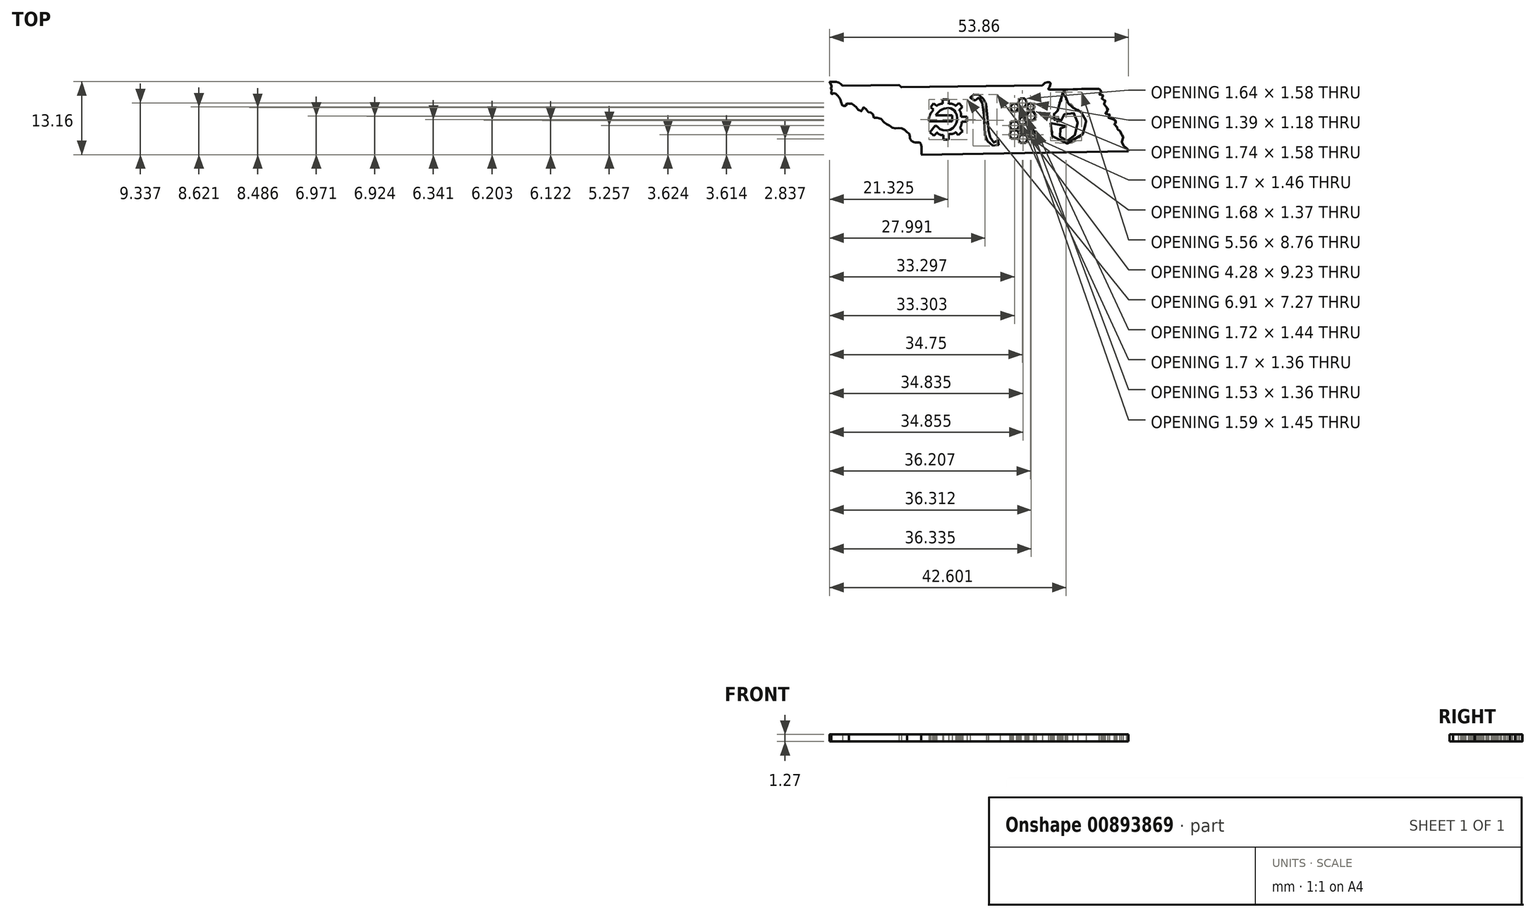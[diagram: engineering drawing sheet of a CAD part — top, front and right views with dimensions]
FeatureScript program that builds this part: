
annotation { "Feature Type Name" : "Feature", "Feature Type Description" : "" }
export const myFeature = defineFeature(function(context is Context, id is Id, definition is map)
    precondition{}
    {
        {
            var Q0;
            Q0=qCreatedBy(makeId("Top.planeOp"),FACE);
            var sketch = newSketch(context, id + "F0", { "sketchPlane" : qUnion([Q0])});
            skLineSegment(sketch, "E0", {"start": v(-39.27, 28.7) * mm, "end": v(-40.07, 28.7) * mm});
            skLineSegment(sketch, "E1", {"start": v(-40.07, 28.7) * mm, "end": v(-40.5, 27.94) * mm});
            skLineSegment(sketch, "E2", {"start": v(-40.5, 27.94) * mm, "end": v(-40.07, 27.12) * mm});
            skLineSegment(sketch, "E3", {"start": v(-39.27, 28.7) * mm, "end": v(-38.86, 27.94) * mm});
            skLineSegment(sketch, "E4", {"start": v(-38.86, 27.94) * mm, "end": v(-39.27, 27.22) * mm});
            skLineSegment(sketch, "E5", {"start": v(-40.07, 27.12) * mm, "end": v(-39.27, 27.22) * mm});
            skLineSegment(sketch, "E6", {"start": v(-40.69, 27.78) * mm, "end": v(-40.34, 27.12) * mm});
            skLineSegment(sketch, "E7", {"start": v(-40.34, 27.12) * mm, "end": v(-40.79, 26.33) * mm});
            skLineSegment(sketch, "E8", {"start": v(-40.69, 27.78) * mm, "end": v(-41.36, 27.78) * mm});
            skLineSegment(sketch, "E9", {"start": v(-41.36, 27.78) * mm, "end": v(-41.93, 27.12) * mm});
            skLineSegment(sketch, "E10", {"start": v(-41.93, 27.12) * mm, "end": v(-41.52, 26.33) * mm});
            skLineSegment(sketch, "E11", {"start": v(-40.79, 26.33) * mm, "end": v(-41.52, 26.33) * mm});
            skLineSegment(sketch, "E12", {"start": v(-37.75, 27.78) * mm, "end": v(-38.6, 27.78) * mm});
            skLineSegment(sketch, "E13", {"start": v(-38.6, 27.78) * mm, "end": v(-38.92, 27.22) * mm});
            skLineSegment(sketch, "E14", {"start": v(-38.92, 27.22) * mm, "end": v(-38.6, 26.6) * mm});
            skLineSegment(sketch, "E15", {"start": v(-37.75, 27.78) * mm, "end": v(-37.53, 27.22) * mm});
            skLineSegment(sketch, "E16", {"start": v(-37.53, 27.22) * mm, "end": v(-37.75, 26.64) * mm});
            skLineSegment(sketch, "E17", {"start": v(-37.75, 26.64) * mm, "end": v(-38.6, 26.6) * mm});
            skLineSegment(sketch, "E18", {"start": v(-37.75, 26.33) * mm, "end": v(-38.6, 26.3) * mm});
            skLineSegment(sketch, "E19", {"start": v(-37.75, 26.33) * mm, "end": v(-37.25, 25.55) * mm});
            skLineSegment(sketch, "E20", {"start": v(-38.6, 26.3) * mm, "end": v(-39, 25.6) * mm});
            skLineSegment(sketch, "E21", {"start": v(-37.25, 25.55) * mm, "end": v(-37.7, 24.75) * mm});
            skLineSegment(sketch, "E22", {"start": v(-39, 25.6) * mm, "end": v(-38.67, 24.76) * mm});
            skLineSegment(sketch, "E23", {"start": v(-37.7, 24.75) * mm, "end": v(-38.67, 24.76) * mm});
            skLineSegment(sketch, "E24", {"start": v(-39.11, 25.37) * mm, "end": v(-38.83, 24.63) * mm});
            skPoint(sketch, "E24.endSnap0", {"position": v(-38.83, 25.18) * mm});
            skLineSegment(sketch, "E25", {"start": v(-38.83, 24.63) * mm, "end": v(-39.18, 24.01) * mm});
            skLineSegment(sketch, "E26", {"start": v(-39.11, 25.37) * mm, "end": v(-39.94, 25.37) * mm});
            skLineSegment(sketch, "E27", {"start": v(-39.94, 25.37) * mm, "end": v(-40.36, 24.63) * mm});
            skLineSegment(sketch, "E28", {"start": v(-40.36, 24.63) * mm, "end": v(-40.13, 24.03) * mm});
            skLineSegment(sketch, "E29", {"start": v(-39.18, 24.01) * mm, "end": v(-40.13, 24.03) * mm});
            skLineSegment(sketch, "E30", {"start": v(-40.54, 24.5) * mm, "end": v(-40.28, 23.82) * mm});
            skLineSegment(sketch, "E31", {"start": v(-40.28, 23.82) * mm, "end": v(-40.6, 23.2) * mm});
            skLineSegment(sketch, "E32", {"start": v(-40.54, 24.5) * mm, "end": v(-41.6, 24.5) * mm});
            skLineSegment(sketch, "E33", {"start": v(-41.6, 24.5) * mm, "end": v(-41.98, 23.82) * mm});
            skLineSegment(sketch, "E34", {"start": v(-41.98, 23.82) * mm, "end": v(-41.72, 23.15) * mm});
            skLineSegment(sketch, "E35", {"start": v(-40.6, 23.2) * mm, "end": v(-41.72, 23.15) * mm});
            skLineSegment(sketch, "E36", {"start": v(-40.6, 22.92) * mm, "end": v(-41.72, 22.85) * mm});
            skLineSegment(sketch, "E37", {"start": v(-40.6, 22.92) * mm, "end": v(-40.28, 22.3) * mm});
            skLineSegment(sketch, "E38", {"start": v(-40.28, 22.3) * mm, "end": v(-40.6, 21.47) * mm});
            skLineSegment(sketch, "E39", {"start": v(-41.72, 22.85) * mm, "end": v(-41.98, 22.15) * mm});
            skLineSegment(sketch, "E40", {"start": v(-41.98, 22.15) * mm, "end": v(-41.72, 21.47) * mm});
            skLineSegment(sketch, "E41", {"start": v(-40.6, 21.47) * mm, "end": v(-41.72, 21.47) * mm});
            skLineSegment(sketch, "E42", {"start": v(-39.08, 22.1) * mm, "end": v(-40.08, 22.1) * mm});
            skLineSegment(sketch, "E43", {"start": v(-40.08, 22.1) * mm, "end": v(-40.41, 21.36) * mm});
            skLineSegment(sketch, "E44", {"start": v(-40.41, 21.36) * mm, "end": v(-40.08, 20.73) * mm});
            skLineSegment(sketch, "E45", {"start": v(-39.08, 22.1) * mm, "end": v(-38.74, 21.47) * mm});
            skLineSegment(sketch, "E46", {"start": v(-38.74, 21.47) * mm, "end": v(-39.08, 20.72) * mm});
            skLineSegment(sketch, "E47", {"start": v(-39.08, 20.72) * mm, "end": v(-40.08, 20.73) * mm});
            skLineSegment(sketch, "E48", {"start": v(-37.57, 22.9) * mm, "end": v(-37.24, 22.24) * mm});
            skLineSegment(sketch, "E49", {"start": v(-37.24, 22.24) * mm, "end": v(-37.63, 21.47) * mm});
            skLineSegment(sketch, "E50", {"start": v(-37.57, 22.9) * mm, "end": v(-38.55, 22.9) * mm});
            skLineSegment(sketch, "E51", {"start": v(-38.55, 22.9) * mm, "end": v(-38.95, 22.17) * mm});
            skLineSegment(sketch, "E52", {"start": v(-38.95, 22.17) * mm, "end": v(-38.6, 21.5) * mm});
            skLineSegment(sketch, "E53", {"start": v(-37.63, 21.47) * mm, "end": v(-38.6, 21.5) * mm});
            skLineSegment(sketch, "E54", {"start": v(-52.37, 25.66) * mm, "end": v(-52.37, 24.59) * mm});
            skLineSegment(sketch, "E55", {"start": v(-52.37, 25.66) * mm, "end": v(-55.36, 25.66) * mm});
            skLineSegment(sketch, "E56", {"start": v(-52.37, 24.59) * mm, "end": v(-56.43, 24.59) * mm});
            skFitSpline(sketch, "E57", {"points": [v(-56.43, 24.59) * mm, v(-56.54, 24.72) * mm, v(-56.43, 25.58) * mm, v(-55.9, 26.42) * mm], "startDerivative": vector(-0.75, 0.5) * mm, "endDerivative": vector(1.41, 1.79) * mm});
            skLineSegment(sketch, "E58", {"start": v(-55.13, 27.37) * mm, "end": v(-55.68, 27.8) * mm});
            skLineSegment(sketch, "E59", {"start": v(-55.68, 27.8) * mm, "end": v(-56.24, 27.1) * mm});
            skLineSegment(sketch, "E60", {"start": v(-56.24, 27.1) * mm, "end": v(-55.73, 26.7) * mm});
            skLineSegment(sketch, "E61", {"start": v(-52.97, 27.73) * mm, "end": v(-52.97, 28.54) * mm});
            skLineSegment(sketch, "E62", {"start": v(-52.97, 28.54) * mm, "end": v(-54.04, 28.54) * mm});
            skLineSegment(sketch, "E63", {"start": v(-54.04, 28.54) * mm, "end": v(-54.04, 27.75) * mm});
            skLineSegment(sketch, "E64", {"start": v(-50.5, 27.18) * mm, "end": v(-51.09, 26.62) * mm});
            skLineSegment(sketch, "E65", {"start": v(-50.5, 27.18) * mm, "end": v(-51.16, 27.88) * mm});
            skLineSegment(sketch, "E66", {"start": v(-51.16, 27.88) * mm, "end": v(-51.72, 27.35) * mm});
            skLineSegment(sketch, "E67", {"start": v(-49.65, 25.43) * mm, "end": v(-49.65, 24.53) * mm});
            skLineSegment(sketch, "E68", {"start": v(-49.65, 24.53) * mm, "end": v(-50.33, 24.53) * mm});
            skLineSegment(sketch, "E69", {"start": v(-49.65, 25.43) * mm, "end": v(-50.32, 25.43) * mm});
            skLineSegment(sketch, "E70", {"start": v(-50.93, 23.39) * mm, "end": v(-50.46, 22.78) * mm});
            skLineSegment(sketch, "E71", {"start": v(-50.46, 22.78) * mm, "end": v(-51.29, 22.13) * mm});
            skLineSegment(sketch, "E72", {"start": v(-51.29, 22.13) * mm, "end": v(-51.69, 22.65) * mm});
            skLineSegment(sketch, "E73", {"start": v(-52.99, 22.09) * mm, "end": v(-52.99, 21.28) * mm});
            skLineSegment(sketch, "E74", {"start": v(-52.99, 21.28) * mm, "end": v(-53.96, 21.28) * mm});
            skLineSegment(sketch, "E75", {"start": v(-53.96, 21.28) * mm, "end": v(-53.96, 22.1) * mm});
            skLineSegment(sketch, "E76", {"start": v(-55.12, 22.5) * mm, "end": v(-55.63, 21.98) * mm});
            skLineSegment(sketch, "E77", {"start": v(-55.63, 21.98) * mm, "end": v(-56.37, 22.6) * mm});
            skLineSegment(sketch, "E78", {"start": v(-56.37, 22.6) * mm, "end": v(-55.38, 23.8) * mm});
            skFitSpline(sketch, "E79", {"points": [v(-55.73, 26.7) * mm, v(-55.9, 26.42) * mm], "startDerivative": vector(-0.18, -0.28) * mm, "endDerivative": vector(-0.18, -0.28) * mm});
            skFitSpline(sketch, "E80", {"points": [v(-54.04, 27.75) * mm, v(-54.32, 27.75) * mm, v(-54.62, 27.66) * mm, v(-54.9, 27.54) * mm, v(-55.13, 27.37) * mm], "startDerivative": vector(-1.13, 0.08) * mm, "endDerivative": vector(-0.94, -0.73) * mm});
            skPoint(sketch, "E81.2.internal.snap0", {"position": v(-50.83, 27.53) * mm});
            skFitSpline(sketch, "E81", {"points": [v(-51.72, 27.35) * mm, v(-51.83, 27.46) * mm, v(-51.94, 27.53) * mm, v(-52.16, 27.64) * mm, v(-52.51, 27.75) * mm, v(-52.76, 27.75) * mm, v(-52.97, 27.73) * mm], "startDerivative": vector(-0.84, 0.83) * mm, "endDerivative": vector(-1.27, -0.15) * mm});
            skFitSpline(sketch, "E82", {"points": [v(-51.09, 26.62) * mm, v(-50.99, 26.52) * mm, v(-50.93, 26.43) * mm, v(-50.87, 26.32) * mm, v(-50.82, 26.17) * mm, v(-50.78, 26) * mm, v(-50.77, 25.83) * mm, v(-50.75, 25.66) * mm, v(-50.75, 25.53) * mm, v(-50.76, 25.43) * mm], "startDerivative": vector(0.92, -0.94) * mm, "endDerivative": vector(-0.13, -1.07) * mm});
            skLineSegment(sketch, "E83", {"start": v(-50.32, 25.43) * mm, "end": v(-50.76, 25.43) * mm});
            skLineSegment(sketch, "E84", {"start": v(-50.33, 24.53) * mm, "end": v(-50.6, 24.53) * mm});
            skFitSpline(sketch, "E85", {"points": [v(-50.6, 24.53) * mm, v(-50.6, 24.48) * mm, v(-50.6, 24.42) * mm, v(-50.6, 24.34) * mm, v(-50.63, 24.21) * mm, v(-50.66, 24.13) * mm, v(-50.67, 24) * mm, v(-50.7, 23.9) * mm, v(-50.77, 23.76) * mm, v(-50.8, 23.67) * mm, v(-50.85, 23.57) * mm, v(-50.9, 23.5) * mm, v(-50.9, 23.45) * mm, v(-50.93, 23.39) * mm], "startDerivative": vector(0, -0.85) * mm, "endDerivative": vector(-0.45, -0.89) * mm});
            skFitSpline(sketch, "E86", {"points": [v(-51.69, 22.65) * mm, v(-51.76, 22.58) * mm, v(-51.9, 22.46) * mm, v(-52.11, 22.36) * mm, v(-52.38, 22.29) * mm, v(-52.65, 22.29) * mm, v(-52.85, 22.33) * mm, v(-52.99, 22.09) * mm], "startDerivative": vector(-0.64, -0.65) * mm, "endDerivative": vector(-0.73, -1.97) * mm});
            skFitSpline(sketch, "E87", {"points": [v(-53.96, 22.1) * mm, v(-54.08, 22.1) * mm, v(-54.3, 22.1) * mm, v(-54.53, 22.17) * mm, v(-54.72, 22.26) * mm, v(-54.93, 22.41) * mm, v(-55.06, 22.56) * mm, v(-55.12, 22.5) * mm], "startDerivative": vector(-0.95, 0.02) * mm, "endDerivative": vector(-0.68, -0.94) * mm});
            skFitSpline(sketch, "E88", {"points": [v(-55.38, 23.8) * mm, v(-55.3, 23.9) * mm, v(-55.23, 23.93) * mm, v(-55.12, 23.8) * mm, v(-54.98, 23.62) * mm, v(-54.84, 23.47) * mm, v(-54.76, 23.39) * mm, v(-54.63, 23.24) * mm, v(-54.52, 23.17) * mm, v(-54.39, 23.1) * mm, v(-54.25, 23.04) * mm, v(-54.06, 22.99) * mm, v(-53.85, 22.96) * mm, v(-53.6, 22.93) * mm, v(-53.4, 22.95) * mm, v(-53.23, 22.97) * mm, v(-53.05, 23) * mm, v(-52.85, 23.03) * mm, v(-52.7, 23.05) * mm, v(-52.5, 23.1) * mm, v(-52.4, 23.17) * mm, v(-52.28, 23.25) * mm, v(-52.15, 23.39) * mm, v(-52, 23.53) * mm, v(-51.9, 23.68) * mm, v(-51.82, 23.8) * mm, v(-51.76, 23.93) * mm, v(-51.69, 24.08) * mm, v(-51.65, 24.19) * mm, v(-51.61, 24.3) * mm, v(-51.56, 24.44) * mm, v(-51.53, 24.53) * mm, v(-51.5, 24.64) * mm, v(-51.5, 24.72) * mm, v(-51.48, 24.8) * mm, v(-51.47, 24.9) * mm, v(-51.47, 24.98) * mm, v(-51.47, 25.09) * mm, v(-51.48, 25.17) * mm, v(-51.48, 25.23) * mm, v(-51.5, 25.32) * mm, v(-51.5, 25.4) * mm, v(-51.51, 25.53) * mm, v(-51.52, 25.66) * mm, v(-51.57, 25.81) * mm, v(-51.6, 25.97) * mm, v(-51.69, 26.13) * mm, v(-51.73, 26.2) * mm, v(-51.75, 26.24) * mm, v(-51.78, 26.3) * mm, v(-51.8, 26.34) * mm, v(-51.83, 26.38) * mm, v(-51.88, 26.43) * mm, v(-51.94, 26.5) * mm, v(-51.98, 26.54) * mm, v(-52.03, 26.59) * mm, v(-52.08, 26.63) * mm, v(-52.15, 26.68) * mm, v(-52.2, 26.7) * mm, v(-52.25, 26.74) * mm, v(-52.29, 26.76) * mm, v(-52.35, 26.8) * mm, v(-52.4, 26.82) * mm, v(-52.45, 26.85) * mm, v(-52.5, 26.88) * mm, v(-52.6, 26.92) * mm, v(-52.66, 26.94) * mm, v(-52.73, 26.96) * mm, v(-52.81, 26.96) * mm, v(-52.9, 26.97) * mm, v(-52.97, 26.98) * mm, v(-53.05, 26.99) * mm, v(-53.13, 26.98) * mm, v(-53.17, 26.98) * mm, v(-53.25, 26.97) * mm, v(-53.3, 26.96) * mm, v(-53.38, 26.95) * mm, v(-53.42, 26.95) * mm, v(-53.5, 26.93) * mm, v(-53.56, 26.92) * mm, v(-53.62, 26.9) * mm, v(-53.7, 26.9) * mm, v(-53.78, 26.87) * mm, v(-53.84, 26.85) * mm, v(-53.9, 26.83) * mm, v(-53.98, 26.8) * mm, v(-54.02, 26.79) * mm, v(-54.09, 26.76) * mm, v(-54.15, 26.74) * mm, v(-54.2, 26.71) * mm, v(-54.26, 26.68) * mm, v(-54.32, 26.66) * mm, v(-54.39, 26.61) * mm, v(-54.45, 26.57) * mm, v(-54.5, 26.52) * mm, v(-54.55, 26.5) * mm, v(-54.61, 26.46) * mm, v(-54.67, 26.42) * mm, v(-54.7, 26.38) * mm, v(-54.75, 26.34) * mm, v(-54.8, 26.3) * mm, v(-54.84, 26.26) * mm, v(-54.9, 26.21) * mm, v(-54.95, 26.16) * mm, v(-55, 26.1) * mm, v(-55.08, 26) * mm, v(-55.18, 25.89) * mm, v(-55.2, 25.84) * mm, v(-55.26, 25.78) * mm, v(-55.3, 25.72) * mm, v(-55.36, 25.66) * mm], "startDerivative": vector(7.58, 10.82) * mm, "endDerivative": vector(-6.43, -7.93) * mm});
            skPoint(sketch, "E89.35.internal.snap0", {"position": v(-49.65, 24.98) * mm});
            skPoint(sketch, "E89.80.internal.snap0", {"position": v(-49.65, 24.98) * mm});
            skFitSpline(sketch, "E89", {"points": [v(-47.5, 28.9) * mm, v(-47.69, 28.99) * mm, v(-47.87, 28.93) * mm, v(-47.92, 28.66) * mm, v(-48.16, 28.37) * mm, v(-48.48, 28.32) * mm, v(-48.77, 28.38) * mm, v(-49.01, 28.59) * mm, v(-49.08, 28.79) * mm, v(-49.04, 29.03) * mm, v(-48.97, 29.15) * mm, v(-48.85, 29.29) * mm, v(-48.74, 29.36) * mm, v(-48.52, 29.4) * mm, v(-48.4, 29.44) * mm, v(-48.18, 29.44) * mm, v(-47.97, 29.43) * mm, v(-47.73, 29.39) * mm, v(-47.53, 29.32) * mm, v(-47.36, 29.25) * mm, v(-47.15, 29.03) * mm, v(-46.97, 28.9) * mm, v(-46.77, 28.63) * mm, v(-46.58, 28.43) * mm, v(-46.48, 28.28) * mm, v(-46.39, 28.06) * mm, v(-46.3, 27.86) * mm, v(-46.24, 27.63) * mm, v(-46.17, 27.29) * mm, v(-46.16, 26.93) * mm, v(-46.11, 26.7) * mm, v(-46.1, 26.3) * mm, v(-46.08, 26.08) * mm, v(-46.04, 25.66) * mm, v(-46.04, 25.43) * mm, v(-46, 24.98) * mm, v(-45.96, 24.64) * mm, v(-45.94, 24.42) * mm, v(-45.88, 24.07) * mm, v(-45.88, 23.8) * mm, v(-45.84, 23.55) * mm, v(-45.84, 23.39) * mm, v(-45.8, 23.1) * mm, v(-45.76, 22.78) * mm, v(-45.72, 22.29) * mm, v(-45.62, 21.98) * mm, v(-45.5, 21.67) * mm, v(-45.37, 21.36) * mm, v(-45.16, 21) * mm, v(-44.93, 20.66) * mm, v(-44.83, 20.87) * mm, v(-44.72, 21) * mm, v(-44.6, 21.1) * mm, v(-44.37, 21.14) * mm, v(-44.18, 21.16) * mm, v(-43.96, 21.11) * mm, v(-43.8, 21.01) * mm, v(-43.72, 20.78) * mm, v(-43.82, 20.5) * mm, v(-44.03, 20.3) * mm, v(-44.2, 20.18) * mm, v(-44.48, 20.16) * mm, v(-44.83, 20.2) * mm, v(-45.05, 20.23) * mm, v(-45.32, 20.4) * mm, v(-45.58, 20.62) * mm, v(-45.88, 20.88) * mm, v(-46.03, 21.11) * mm, v(-46.18, 21.36) * mm, v(-46.3, 21.65) * mm, v(-46.39, 21.98) * mm, v(-46.45, 22.5) * mm, v(-46.45, 22.65) * mm, v(-46.47, 23.1) * mm, v(-46.5, 23.58) * mm, v(-46.5, 23.68) * mm, v(-46.5, 23.93) * mm, v(-46.53, 24.16) * mm, v(-46.55, 24.42) * mm, v(-46.56, 24.64) * mm, v(-46.57, 24.98) * mm, v(-46.6, 25.28) * mm, v(-46.61, 25.53) * mm, v(-46.64, 25.77) * mm, v(-46.67, 25.98) * mm, v(-46.7, 26.2) * mm, v(-46.74, 26.41) * mm, v(-46.77, 26.57) * mm, v(-46.8, 26.96) * mm, v(-46.85, 27.42) * mm, v(-46.9, 27.7) * mm, v(-46.97, 28.02) * mm, v(-47.1, 28.3) * mm, v(-47.2, 28.48) * mm, v(-47.35, 28.72) * mm, v(-47.5, 28.9) * mm]});
            skLineSegment(sketch, "E90", {"start": v(-31.8, 23.69) * mm, "end": v(-34.6, 24.27) * mm});
            skFitSpline(sketch, "E91", {"points": [v(-31.8, 23.69) * mm, v(-31.63, 23.48) * mm, v(-31.8, 23.42) * mm, v(-32.27, 23.46) * mm, v(-32.54, 23.47) * mm, v(-32.84, 23.34) * mm, v(-32.9, 23.22) * mm, v(-32.9, 22.78) * mm, v(-32.93, 22.54) * mm, v(-32.9, 22.2) * mm, v(-32.9, 21.77) * mm, v(-32.78, 21.59) * mm, v(-32.5, 21.36) * mm, v(-32.1, 21.16) * mm, v(-31.92, 21.13) * mm, v(-31.6, 21.08) * mm, v(-31.32, 21.12) * mm, v(-30.92, 21.36) * mm, v(-30.6, 21.6) * mm, v(-30.31, 22) * mm, v(-30.07, 22.42) * mm, v(-29.86, 23.18) * mm, v(-29.77, 23.92) * mm, v(-29.77, 24.48) * mm, v(-29.87, 24.92) * mm, v(-30.05, 25.45) * mm, v(-30.24, 25.83) * mm, v(-30.53, 26.14) * mm, v(-30.86, 26.2) * mm, v(-31.43, 26.21) * mm, v(-31.8, 25.98) * mm, v(-32.27, 25.78) * mm, v(-32.42, 25.54) * mm, v(-32.41, 25.39) * mm, v(-32.65, 25.29) * mm, v(-32.61, 25.06) * mm, v(-32.7, 24.78) * mm, v(-32.83, 24.46) * mm, v(-33.06, 24.4) * mm, v(-33.27, 24.45) * mm, v(-33.42, 24.53) * mm, v(-33.38, 24.72) * mm, v(-33.21, 25.03) * mm, v(-33.13, 25.17) * mm, v(-33.16, 25.41) * mm, v(-33.39, 25.37) * mm, v(-33.61, 25.2) * mm, v(-33.9, 24.81) * mm, v(-34.32, 24.86) * mm, v(-34.4, 25.17) * mm, v(-34.13, 25.46) * mm, v(-33.96, 25.66) * mm, v(-34.05, 25.97) * mm, v(-33.97, 26.2) * mm, v(-33.8, 26.13) * mm, v(-33.58, 26.07) * mm, v(-33.39, 26.08) * mm, v(-33.33, 26.3) * mm, v(-33.27, 26.75) * mm, v(-33.1, 26.88) * mm, v(-33.14, 27.37) * mm, v(-33.05, 27.82) * mm, v(-32.9, 28.1) * mm, v(-32.73, 28.22) * mm, v(-32.7, 28.45) * mm, v(-32.63, 28.9) * mm, v(-32.54, 29.23) * mm, v(-32.46, 29.72) * mm, v(-32.43, 29.83) * mm, v(-32.13, 29.88) * mm, v(-31.8, 29.81) * mm, v(-31.8, 29.48) * mm, v(-31.99, 28.28) * mm, v(-31.8, 28.04) * mm, v(-31.57, 27.98) * mm, v(-31.61, 27.7) * mm, v(-31.5, 27.8) * mm, v(-31.24, 27.86) * mm, v(-30.98, 27.8) * mm, v(-30.78, 27.73) * mm, v(-30.63, 27.5) * mm, v(-30.6, 27.25) * mm, v(-30.6, 27.04) * mm, v(-30.39, 27.09) * mm, v(-29.75, 26.9) * mm, v(-29.43, 26.59) * mm, v(-29.13, 26.24) * mm, v(-28.91, 25.9) * mm, v(-28.7, 25.53) * mm, v(-28.43, 25.13) * mm, v(-28.25, 24.74) * mm, v(-28.24, 24.3) * mm, v(-28.31, 23.5) * mm, v(-28.58, 22.7) * mm, v(-29.37, 21.58) * mm, v(-30.5, 20.74) * mm, v(-32.74, 20.58) * mm, v(-34.17, 20.93) * mm, v(-34.23, 22.43) * mm, v(-34.28, 23.69) * mm, v(-34.7, 24.04) * mm, v(-34.6, 24.27) * mm], "startDerivative": vector(32.1, -28.56) * mm, "endDerivative": vector(24.42, 30.36) * mm});
            skFitSpline(sketch, "E92", {"points": [v(-25.85, 30.42) * mm, v(-27.64, 30.42) * mm, v(-30.26, 30.37) * mm, v(-34.8, 30.3) * mm, v(-35.02, 30.39) * mm, v(-34.85, 30.74) * mm, v(-34.65, 31.5) * mm, v(-35.39, 31.6) * mm, v(-36.08, 31.06) * mm, v(-35.98, 31.07) * mm], "startDerivative": vector(-12.28, 0) * mm, "endDerivative": vector(3.97, 1.07) * mm});
            skLineSegment(sketch, "E93", {"start": v(-36.03, 31.06) * mm, "end": v(-61.52, 30.74) * mm});
            skFitSpline(sketch, "E94", {"points": [v(-61.52, 30.74) * mm, v(-61.96, 31.15) * mm, v(-62.02, 31.2) * mm], "startDerivative": vector(-0.74, 0.7) * mm, "endDerivative": vector(-0.18, 0.12) * mm});
            skLineSegment(sketch, "E95", {"start": v(-61.96, 31.15) * mm, "end": v(-67.77, 31.08) * mm});
            skLineSegment(sketch, "E96", {"start": v(-67.77, 31.08) * mm, "end": v(-72.11, 31.03) * mm});
            skFitSpline(sketch, "E97", {"points": [v(-72.11, 31.03) * mm, v(-72.6, 31.47) * mm, v(-73.24, 31.72) * mm, v(-74, 31.7) * mm, v(-74.43, 31.68) * mm, v(-74.05, 31.03) * mm, v(-74.22, 30.65) * mm, v(-74.06, 30.14) * mm, v(-74.14, 29.5) * mm, v(-73.68, 29.64) * mm, v(-73.24, 29.49) * mm, v(-72.71, 28.86) * mm, v(-72.4, 28.32) * mm, v(-72.11, 27.42) * mm, v(-71.55, 27.42) * mm, v(-71.29, 27.78) * mm, v(-70.93, 27.78) * mm], "startDerivative": vector(-6.91, 7.27) * mm, "endDerivative": vector(8.39, -1.92) * mm});
            skFitSpline(sketch, "E98", {"points": [v(-70.93, 27.78) * mm, v(-70.44, 27.78) * mm, v(-70, 27.42) * mm, v(-69.6, 27.12) * mm, v(-69.28, 26.68) * mm, v(-68.64, 26.41) * mm, v(-68.51, 26.68) * mm, v(-68.33, 27.12) * mm, v(-67.84, 26.68) * mm, v(-67.38, 26.2) * mm, v(-67, 26.2) * mm, v(-66.62, 25.8) * mm, v(-66.35, 25.18) * mm, v(-65.45, 25.18) * mm, v(-64.59, 24.35) * mm, v(-64.1, 24.03) * mm, v(-63.45, 23.68) * mm, v(-62.88, 23.33) * mm, v(-62.2, 23.37) * mm, v(-61.65, 23.33) * mm, v(-60.99, 23.12) * mm, v(-60.5, 22.6) * mm], "startDerivative": vector(12.1, 2.17) * mm, "endDerivative": vector(8.48, -11.76) * mm});
            skFitSpline(sketch, "E99", {"points": [v(-60.5, 22.6) * mm, v(-60.05, 22.24) * mm, v(-59.9, 21.36) * mm, v(-59.4, 20.88) * mm, v(-58.68, 20.79) * mm, v(-58.16, 20.71) * mm, v(-57.92, 20.13) * mm, v(-57.87, 19.44) * mm, v(-57.89, 18.6) * mm, v(-57.91, 18.57) * mm, v(-57.98, 18.56) * mm], "startDerivative": vector(5.07, -2.48) * mm, "endDerivative": vector(-2.1, 0.06) * mm});
            skLineSegment(sketch, "E100", {"start": v(-57.91, 18.57) * mm, "end": v(-20.57, 19.21) * mm});
            skFitSpline(sketch, "E101", {"points": [v(-25.85, 30.42) * mm, v(-25.5, 30.14) * mm, v(-25.54, 29.83) * mm, v(-25.85, 29.44) * mm, v(-25.26, 29.42) * mm, v(-25.25, 28.97) * mm, v(-25.38, 28.62) * mm, v(-24.84, 28.47) * mm, v(-24.91, 27.84) * mm, v(-24.97, 27.7) * mm, v(-24.57, 27.17) * mm, v(-24.29, 26.77) * mm, v(-24.5, 26.37) * mm, v(-24.72, 26) * mm, v(-24.34, 25.86) * mm, v(-23.99, 25.77) * mm, v(-24.25, 25.34) * mm, v(-23.41, 24.97) * mm, v(-22.96, 24.79) * mm, v(-22.9, 24.51) * mm, v(-22.96, 24.13) * mm, v(-23.16, 24.04) * mm, v(-22.63, 23.59) * mm, v(-22.69, 23.24) * mm, v(-22.62, 23.14) * mm, v(-22.33, 23.15) * mm, v(-22.14, 22.85) * mm, v(-22.08, 22.44) * mm, v(-21.5, 22.05) * mm, v(-21.65, 21.36) * mm, v(-21.78, 20.68) * mm, v(-21.42, 20.14) * mm, v(-20.8, 19.72) * mm, v(-20.9, 19.5) * mm, v(-20.57, 19.21) * mm], "startDerivative": vector(14.45, -9.02) * mm, "endDerivative": vector(17.28, -10.26) * mm});
            skSolve(sketch);
        }
        {
            var Q0;
            Q0 = qSketchRegion(id + "F0", true);
            extrude(context, id + "F1", {"entities" : qUnion([Q0]), "depth" : 1.27 * mm, "offsetDistance" : 25.4 * mm});
        }
    });
